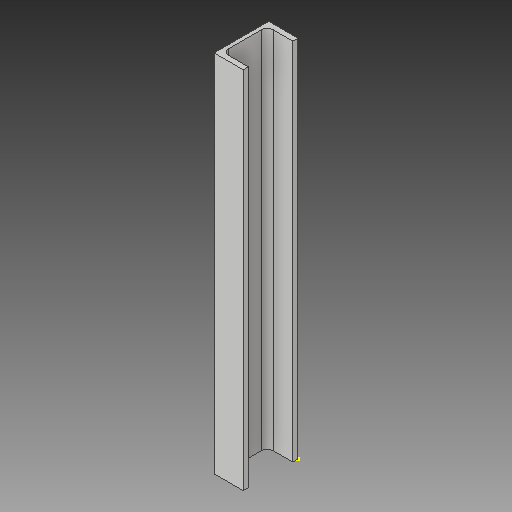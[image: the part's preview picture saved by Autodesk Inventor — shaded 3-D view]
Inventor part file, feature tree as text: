
AUTODESK INVENTOR PART (.ipt)
format: ipt  version: 2019 (Build 230136000, 136)  size: 93,696 bytes
history: native  units: in
note: dims shown in document units (in); Inventor stores cm internally (conversion verified against a paired STEP export)
features: other x3, sketch x2
ambient origin geometry x8: Origin, YZ Plane, XZ Plane, XY Plane, X Axis, Y Axis, Z Axis, Center Point
bodies: Solid1 (feature_tree)
feature tree (5):
  other  "Channel2_MIR_MIR1.ipt"
  other  "Solid1::Channel2_MIR_MIR1.ipt"
  other  "TaggingFeature1"
  sketch  "Sketch1"  dims[d0=0.3937in]
  sketch  "Sketch2"
